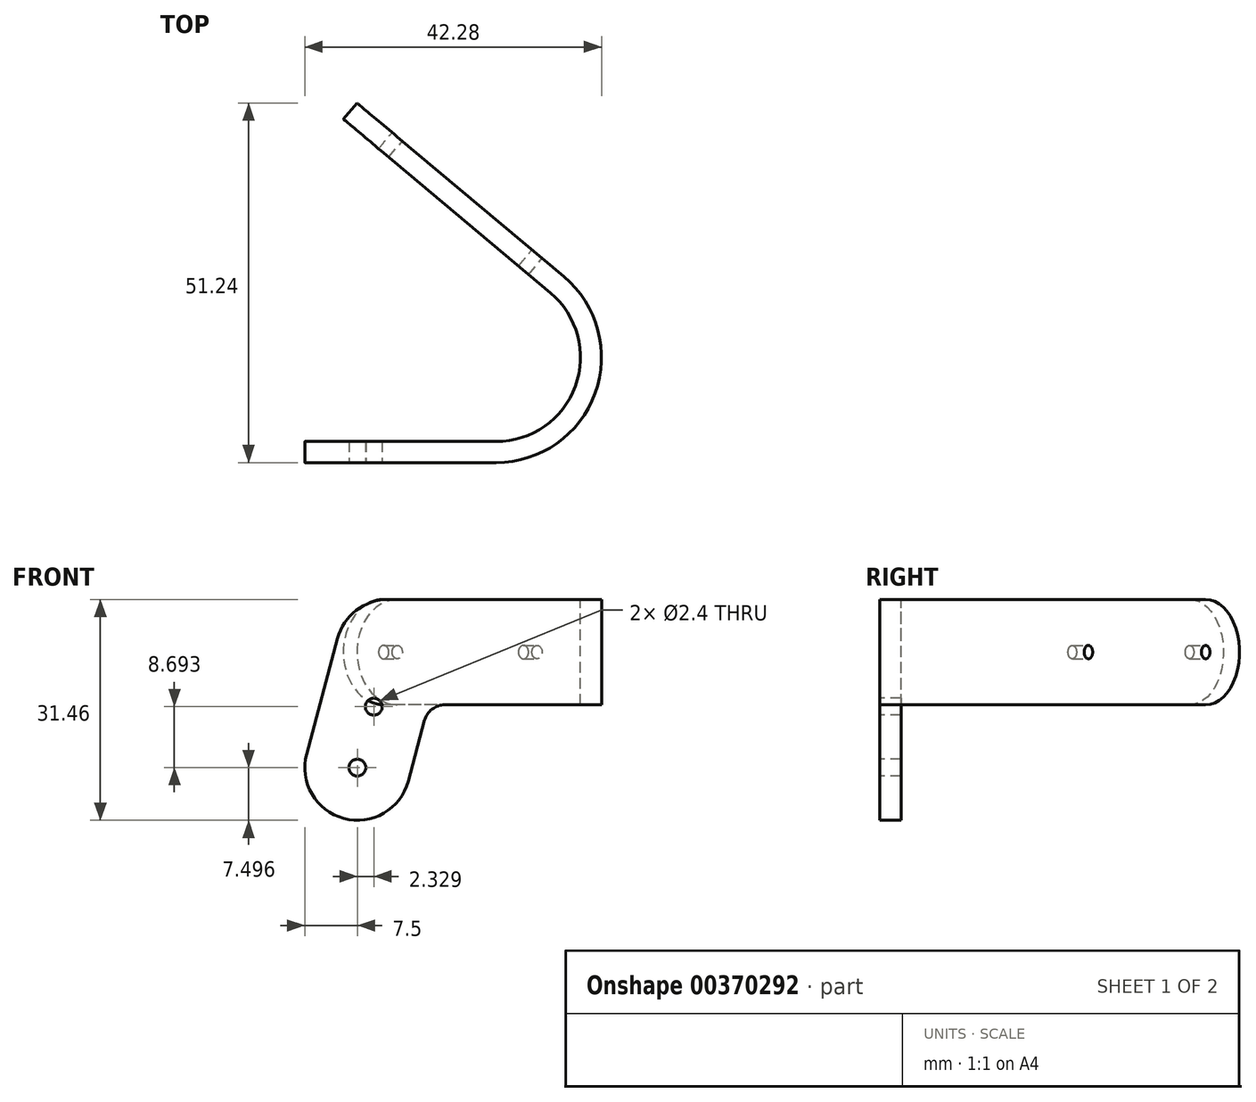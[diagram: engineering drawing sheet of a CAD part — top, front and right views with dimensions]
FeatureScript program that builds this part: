
annotation { "Feature Type Name" : "Feature", "Feature Type Description" : "" }
export const myFeature = defineFeature(function(context is Context, id is Id, definition is map)
    precondition{}
    {
        {
            var Q0;
            Q0=qCreatedBy(makeId("Top.planeOp"),FACE);
            var sketch = newSketch(context, id + "F0", { "sketchPlane" : qUnion([Q0])});
            skLineSegment(sketch, "E0.bottom", {"start": v(-58.64, -28.47) * mm, "end": v(123, -28.47) * mm});
            skLineSegment(sketch, "E0.top", {"start": v(-58.64, 130.62) * mm, "end": v(123, 130.62) * mm});
            skLineSegment(sketch, "E0.left", {"start": v(-58.64, -28.47) * mm, "end": v(-58.64, 130.62) * mm});
            skLineSegment(sketch, "E0.right", {"start": v(123, -28.47) * mm, "end": v(123, 130.62) * mm});
            skLineSegment(sketch, "E1", {"start": v(194.3, 41.37) * mm, "end": v(212.32, 28.75) * mm});
            skLineSegment(sketch, "E2", {"start": v(183.43, 8.54) * mm, "end": v(183.43, 37.28) * mm});
            skLineSegment(sketch, "E3", {"start": v(196.02, 43.83) * mm, "end": v(214.04, 31.21) * mm});
            skLineSegment(sketch, "E4", {"start": v(214.04, 31.21) * mm, "end": v(212.32, 28.75) * mm});
            skPoint(sketch, "E5", {"position": v(211.58, 32.93) * mm});
            skPoint(sketch, "E6", {"position": v(199.3, 41.54) * mm});
            skPoint(sketch, "E7.visualSharp", {"position": v(186.43, 46.88) * mm});
            skArc(sketch, "E7.filletArc", {"start": v(194.3, 41.37) * mm, "mid": v(189.12, 41.71) * mm, "end": v(186.43, 37.28) * mm});
            skArc(sketch, "E8", {"start": v(196.02, 43.83) * mm, "mid": v(187.74, 44.37) * mm, "end": v(183.43, 37.28) * mm});
            skLineSegment(sketch, "E9", {"start": v(134.5, 0.54) * mm, "end": v(178.43, 0.54) * mm});
            skLineSegment(sketch, "E10", {"start": v(134.5, 0.54) * mm, "end": v(134.5, 3.54) * mm});
            skLineSegment(sketch, "E11", {"start": v(134.5, 3.54) * mm, "end": v(178.43, 3.54) * mm});
            skPoint(sketch, "E12.visualSharp", {"position": v(183.43, 3.54) * mm});
            skArc(sketch, "E12.filletArc", {"start": v(178.43, 3.54) * mm, "mid": v(181.96, 5) * mm, "end": v(183.43, 8.54) * mm});
            skArc(sketch, "E13", {"start": v(178.43, 0.54) * mm, "mid": v(184.09, 2.88) * mm, "end": v(186.43, 8.54) * mm});
            skLineSegment(sketch, "E14.trimOffspring", {"start": v(186.43, 8.54) * mm, "end": v(186.43, 37.28) * mm});
            skPoint(sketch, "E15.orphan", {"position": v(186.43, 0.54) * mm});
            skLineSegment(sketch, "E16", {"start": v(0, 0) * mm, "end": v(0, 3) * mm});
            skLineSegment(sketch, "E17.top", {"start": v(0, 3) * mm, "end": v(-38.5, 3) * mm});
            skLineSegment(sketch, "E17.right", {"start": v(-38.5, 0) * mm, "end": v(-38.5, 3) * mm});
            skPoint(sketch, "E18.visualSharp", {"position": v(79.82, 0) * mm});
            skPoint(sketch, "E19", {"position": v(-38.5, 0) * mm});
            skLineSegment(sketch, "E20", {"start": v(-2, 48.94) * mm, "end": v(27.5, 24.2) * mm});
            skLineSegment(sketch, "E21", {"start": v(-0.07, 51.24) * mm, "end": v(29.42, 26.5) * mm});
            skPoint(sketch, "E22", {"position": v(5.84, 46.27) * mm});
            skLineSegment(sketch, "E23", {"start": v(-2, 48.94) * mm, "end": v(-0.07, 51.24) * mm});
            skLineSegment(sketch, "E24", {"start": v(0, 0) * mm, "end": v(19.78, 0) * mm});
            skLineSegment(sketch, "E25", {"start": v(0, 3) * mm, "end": v(19.78, 3) * mm});
            skLineSegment(sketch, "E26.bottom", {"start": v(0, 0) * mm, "end": v(-38.5, 0) * mm});
            skArc(sketch, "E27.filletArc", {"start": v(19.78, 3) * mm, "mid": v(31.05, 10.9) * mm, "end": v(27.5, 24.2) * mm});
            skArc(sketch, "E28", {"start": v(19.78, 0) * mm, "mid": v(33.87, 9.87) * mm, "end": v(29.42, 26.5) * mm});
            skPoint(sketch, "E29", {"position": v(25.76, 29.56) * mm});
            skSolve(sketch);
        }
        {
            var Q0;
            Q0=qCreatedBy(makeId("Front.planeOp"),FACE);
            var sketch = newSketch(context, id + "F1", { "sketchPlane" : qUnion([Q0])});
            skPoint(sketch, "E30", {"position": v(0, -32.06) * mm});
            skLineSegment(sketch, "E31", {"start": v(7.24, -34) * mm, "end": v(9.57, -25.33) * mm});
            skLineSegment(sketch, "E32", {"start": v(12.47, -23.1) * mm, "end": v(80.08, -23.1) * mm});
            skArc(sketch, "E33", {"start": v(-7.24, -30.12) * mm, "mid": v(-1.94, -39.3) * mm, "end": v(7.24, -34) * mm});
            skLineSegment(sketch, "E34", {"start": v(0, -32.06) * mm, "end": v(-3.5, -45.1) * mm});
            skLineSegment(sketch, "E35", {"start": v(0, -32.06) * mm, "end": v(2.33, -23.37) * mm});
            skPoint(sketch, "E36", {"position": v(2.33, -23.37) * mm});
            skPoint(sketch, "E37", {"position": v(-3.5, -45.1) * mm});
            skCircle(sketch, "E38", {"center": v(0, -32.06) * mm, "radius": 1.2 * mm});
            skCircle(sketch, "E39", {"center": v(2.33, -23.37) * mm, "radius": 1.2 * mm});
            skLineSegment(sketch, "E40", {"start": v(19.78, -8.1) * mm, "end": v(49.08, -8.1) * mm});
            skLineSegment(sketch, "E41", {"start": v(49.08, -8.1) * mm, "end": v(80.08, -8.1) * mm});
            skPoint(sketch, "E42", {"position": v(34.43, -8.1) * mm});
            skCircle(sketch, "E43", {"center": v(80.08, -15.6) * mm, "radius": 2.15 * mm});
            skPoint(sketch, "E43.centerSnap0", {"position": v(87.58, -15.6) * mm});
            skCircle(sketch, "E44", {"center": v(54.08, -15.6) * mm, "radius": 2.15 * mm});
            skLineSegment(sketch, "E45", {"start": v(-7.24, -30.12) * mm, "end": v(-2.83, -13.66) * mm});
            skArc(sketch, "E46", {"start": v(80.08, -23.1) * mm, "mid": v(87.58, -15.6) * mm, "end": v(80.08, -8.1) * mm});
            skPoint(sketch, "E47.orphan", {"position": v(91.08, -8.1) * mm});
            skPoint(sketch, "E48.orphan", {"position": v(91.08, -23.1) * mm});
            skLineSegment(sketch, "E49", {"start": v(2.33, -23.37) * mm, "end": v(4.41, -15.6) * mm});
            skPoint(sketch, "E50", {"position": v(4.41, -15.6) * mm});
            skArc(sketch, "E51", {"start": v(4.41, -8.1) * mm, "mid": v(-0.16, -9.65) * mm, "end": v(-2.83, -13.66) * mm});
            skLineSegment(sketch, "E52.trimOffspring", {"start": v(4.41, -8.1) * mm, "end": v(19.78, -8.1) * mm});
            skPoint(sketch, "E53.visualSharp", {"position": v(10.17, -23.1) * mm});
            skArc(sketch, "E53.filletArc", {"start": v(12.47, -23.1) * mm, "mid": v(10.64, -23.72) * mm, "end": v(9.57, -25.33) * mm});
            skPoint(sketch, "E54", {"position": v(19.78, -8.1) * mm});
            skSolve(sketch);
        }
        {
            var Q0;
            Q0=qCreatedBy(makeId("Front.planeOp"),FACE);
            cPlane(context, id + "F2", {"entities" : qUnion([Q0]), "cplaneType" : CPlaneType.OFFSET, "offset" : 1 * mm, "width" : 150 * mm, "height" : 150 * mm});
        }
        {
            var Q0;
            Q0=qCreatedBy(id+"F2.planeOp",FACE);
            var sketch = newSketch(context, id + "F3", { "sketchPlane" : qUnion([Q0])});
            skCircle(sketch, "E55", {"center": v(0, -28.2) * mm, "radius": 1.5 * mm});
            skSolve(sketch);
        }
        {
            var Q0;
            Q0=qSketchRegion(id+"F3",true);
            extrude(context, id + "F4", {"entities" : qUnion([Q0]), "depth" : 5 * mm});
        }
        {
            var Q0;
            Q0=qSketchRegion(id+"F1",true);
            extrude(context, id + "F5", {"entities" : qUnion([Q0]), "operationType" : NewBodyOperationType.ADD, "oppositeDirection" : true, "depth" : 25 * mm});
        }
        {
            var Q0;
            Q0=qCreatedBy(makeId("Front.planeOp"),FACE);
            cPlane(context, id + "F6", {"entities" : qUnion([Q0]), "cplaneType" : CPlaneType.OFFSET, "offset" : 25 * mm, "oppositeDirection" : true, "width" : 150 * mm, "height" : 150 * mm});
        }
        {
            var Q0;
            Q0=qCreatedBy(id+"F6.planeOp",FACE);
            var sketch = newSketch(context, id + "F7", { "sketchPlane" : qUnion([Q0])});
            skLineSegment(sketch, "E56.bottom", {"start": v(-26.54, -8.1) * mm, "end": v(61.75, -8.1) * mm});
            skLineSegment(sketch, "E56.top", {"start": v(-26.54, -23.1) * mm, "end": v(61.75, -23.1) * mm});
            skLineSegment(sketch, "E56.left", {"start": v(-26.54, -8.1) * mm, "end": v(-26.54, -23.1) * mm});
            skLineSegment(sketch, "E56.right", {"start": v(61.75, -8.1) * mm, "end": v(61.75, -23.1) * mm});
            skSolve(sketch);
        }
        {
            var Q0;
            Q0=qSketchRegion(id+"F7",true);
            extrude(context, id + "F8", {"entities" : qUnion([Q0]), "operationType" : NewBodyOperationType.ADD, "oppositeDirection" : true, "depth" : 50 * mm});
        }
        {
            var Q0;
            Q0=makeQuery(id+"F0.imprint","IMPRINT",FACE,{"disambiguationData":[TD([[makeQuery(id+"F0.imprint","IMPRINT",EDGE,{"derivedFrom":sQuery(id+"F0.wireOp",EDGE,"E1")}),1.0]])]});
            var Q1;
            Q1=makeQuery(id+"F0.imprint","IMPRINT",FACE,{"disambiguationData":[TD([[makeQuery(id+"F0.imprint","IMPRINT",EDGE,{"derivedFrom":sQuery(id+"F0.wireOp",EDGE,"E0.bottom")}),1.0]])]});
            extrude(context, id + "F9", {"entities" : qUnion([Q0, Q1]), "operationType" : NewBodyOperationType.REMOVE, "endBound" : BoundingType.THROUGH_ALL, "oppositeDirection" : true, "depth" : 25 * mm});
        }
        {
            var Q0;
            Q0=makeQuery(id+"F9.boolean.opBoolean","COPY",FACE,{"derivedFrom":makeQuery(id+"F9.opExtrude","SWEPT_FACE",FACE,{"disambiguationData":[OSD([sQuery(id+"F0.wireOp",EDGE,"E21")])]})});
            var sketch = newSketch(context, id + "F10", { "sketchPlane" : qUnion([Q0])});
            skCircle(sketch, "E57", {"center": v(25.5, -15.6) * mm, "radius": 0.95 * mm});
            skPoint(sketch, "E57.centerSnap0", {"position": v(33, -15.6) * mm});
            skCircle(sketch, "E58", {"center": v(-0.5, -15.6) * mm, "radius": 0.95 * mm});
            skSolve(sketch);
        }
        {
            var Q0;
            Q0=qSketchRegion(id+"F10",true);
            extrude(context, id + "F11", {"entities" : qUnion([Q0]), "operationType" : NewBodyOperationType.REMOVE, "oppositeDirection" : true, "depth" : 5 * mm});
        }
        {
            var Q0;
            Q0=makeQuery(id+"F9.boolean.opBoolean","INTERSECT",EDGE,{"derivedFrom":[makeQuery(id+"F8.boolean.opBoolean","MERGE",FACE,{"derivedFrom":[makeQuery(id+"F5.opExtrude","SWEPT_FACE",FACE,{"disambiguationData":[OSD([sQuery(id+"F1.wireOp",EDGE,"E40"),sQuery(id+"F1.wireOp",EDGE,"E41"),sQuery(id+"F1.wireOp",EDGE,"E52.trimOffspring")])]}),makeQuery(id+"F8.opExtrude","SWEPT_FACE",FACE,{"disambiguationData":[OSD([sQuery(id+"F7.wireOp",EDGE,"E56.bottom")])]})]}),makeQuery(id+"F9.opExtrude","SWEPT_FACE",FACE,{"disambiguationData":[OSD([sQuery(id+"F0.wireOp",EDGE,"E23")])]})]});
            var Q1;
            Q1=makeQuery(id+"F9.boolean.opBoolean","INTERSECT",EDGE,{"derivedFrom":[makeQuery(id+"F8.boolean.opBoolean","MERGE",FACE,{"derivedFrom":[makeQuery(id+"F5.opExtrude","SWEPT_FACE",FACE,{"disambiguationData":[OSD([sQuery(id+"F1.wireOp",EDGE,"E32")])]}),makeQuery(id+"F8.opExtrude","SWEPT_FACE",FACE,{"disambiguationData":[OSD([sQuery(id+"F7.wireOp",EDGE,"E56.top")])]})]}),makeQuery(id+"F9.opExtrude","SWEPT_FACE",FACE,{"disambiguationData":[OSD([sQuery(id+"F0.wireOp",EDGE,"E23")])]})]});
            fillet(context, id + "F12", {"entities" : qUnion([Q0, Q1]), "radius" : 7.5 * mm, "tangentPropagation" : true, "allowEdgeOverflow" : false});
        }
    });
